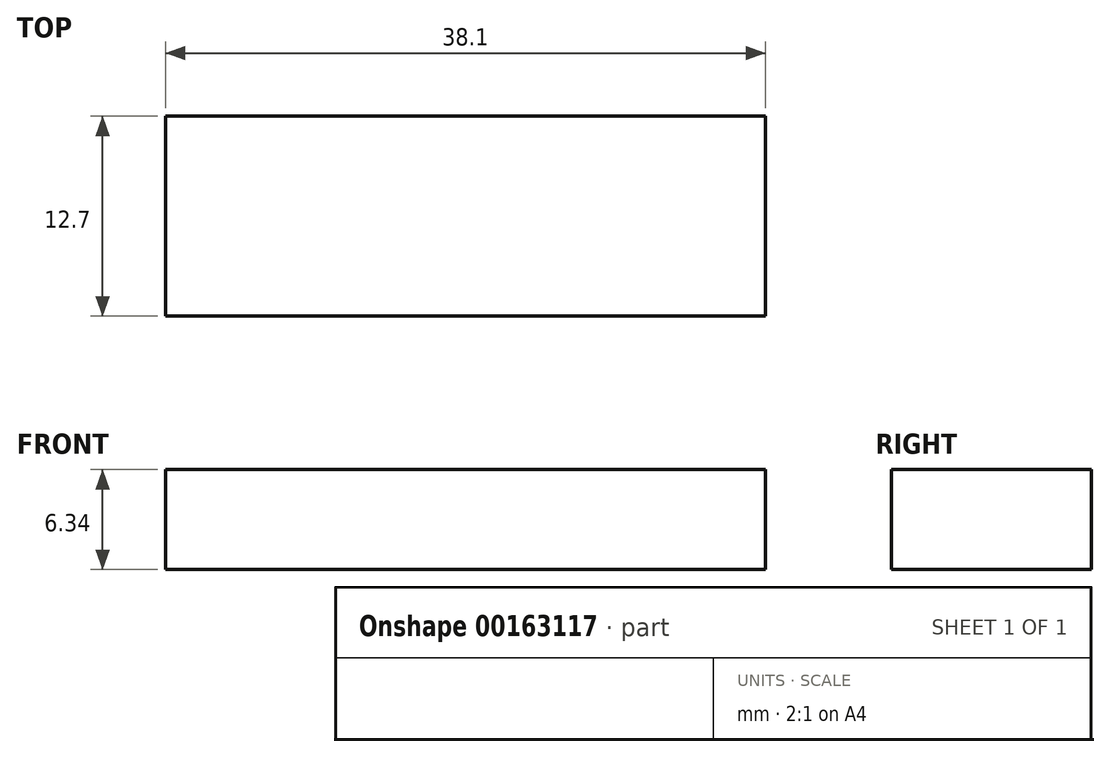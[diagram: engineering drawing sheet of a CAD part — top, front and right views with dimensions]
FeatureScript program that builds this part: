
annotation { "Feature Type Name" : "Feature", "Feature Type Description" : "" }
export const myFeature = defineFeature(function(context is Context, id is Id, definition is map)
    precondition{}
    {
        {
            var Q0;
            Q0=qCreatedBy(makeId("Front.planeOp"),FACE);
            var sketch = newSketch(context, id + "F0", { "sketchPlane" : qUnion([Q0])});
            skLineSegment(sketch, "E0.bottom", {"start": v(19.05, 3.18) * mm, "end": v(-19.05, 3.18) * mm});
            skLineSegment(sketch, "E0.top", {"start": v(19.05, -3.18) * mm, "end": v(-19.05, -3.18) * mm});
            skLineSegment(sketch, "E0.left", {"start": v(19.05, 3.18) * mm, "end": v(19.05, -3.18) * mm});
            skLineSegment(sketch, "E0.right", {"start": v(-19.05, 3.18) * mm, "end": v(-19.05, -3.18) * mm});
            skPoint(sketch, "E0.middle", {"position": v(0, 0) * mm});
            skLineSegment(sketch, "E1", {"start": v(-11, -3.18) * mm, "end": v(-11, -10.8) * mm});
            skLineSegment(sketch, "E2", {"start": v(-11, -10.8) * mm, "end": v(-7.19, -10.8) * mm});
            skLineSegment(sketch, "E3", {"start": v(-7.19, -10.8) * mm, "end": v(-7.19, -3.18) * mm});
            skLineSegment(sketch, "E4", {"start": v(-7.19, -3.18) * mm, "end": v(5.08, -3.18) * mm});
            skLineSegment(sketch, "E5", {"start": v(-14.28, -3.18) * mm, "end": v(-11, -5.44) * mm});
            skLineSegment(sketch, "E6", {"start": v(-11, -5.44) * mm, "end": v(-11, -6.14) * mm});
            skLineSegment(sketch, "E7.0", {"start": v(-16.51, -3.18) * mm, "end": v(-11, -6.98) * mm});
            skLineSegment(sketch, "E8", {"start": v(0, 12.68) * mm, "end": v(0, -18.39) * mm});
            skLineSegment(sketch, "E9.MirrorCS", {"start": v(16.51, -3.18) * mm, "end": v(11, -6.98) * mm});
            skLineSegment(sketch, "E10.MirrorCS", {"start": v(14.28, -3.17) * mm, "end": v(11, -5.44) * mm});
            skLineSegment(sketch, "E11.MirrorCS", {"start": v(7.19, -10.8) * mm, "end": v(7.19, -3.18) * mm});
            skLineSegment(sketch, "E12.MirrorCS", {"start": v(11, -3.18) * mm, "end": v(11, -10.8) * mm});
            skLineSegment(sketch, "E13", {"start": v(7.19, -10.8) * mm, "end": v(11, -10.8) * mm});
            skLineSegment(sketch, "E14", {"start": v(-6.8, 3.18) * mm, "end": v(-6.8, 11.07) * mm});
            skLineSegment(sketch, "E15", {"start": v(-6.8, 11.07) * mm, "end": v(-4.73, 11.07) * mm});
            skLineSegment(sketch, "E16", {"start": v(-4.73, 11.07) * mm, "end": v(-4.73, 3.18) * mm});
            skLineSegment(sketch, "E17", {"start": v(-4.73, 3.18) * mm, "end": v(5.5, 3.18) * mm});
            skLineSegment(sketch, "E18.MirrorCS", {"start": v(4.73, 11.07) * mm, "end": v(4.73, 3.18) * mm});
            skLineSegment(sketch, "E19.MirrorCS", {"start": v(6.8, 11.07) * mm, "end": v(4.73, 11.07) * mm});
            skLineSegment(sketch, "E20.MirrorCS", {"start": v(6.8, 3.18) * mm, "end": v(6.8, 11.07) * mm});
            skSolve(sketch);
        }
        {
            var Q0;
            {var subQ3=sQuery(id+"F0.wireOp",EDGE,"E0.right");Q0=makeQuery(id+"F0.imprint","IMPRINT",FACE,{"disambiguationData":[TD([[makeQuery(id+"F0.imprint","IMPRINT",EDGE,{"derivedFrom":subQ3}),1.0]])]});}
            var Q1;
            {var subQ8=sQuery(id+"F0.wireOp",EDGE,"E0.left");Q1=makeQuery(id+"F0.imprint","IMPRINT",FACE,{"disambiguationData":[TD([[makeQuery(id+"F0.imprint","IMPRINT",EDGE,{"derivedFrom":subQ8}),-1.0]])]});}
            extrude(context, id + "F1", {"entities" : qUnion([Q0, Q1]), "endBound" : BoundingType.SYMMETRIC, "depth" : 12.7 * mm});
        }
    });
